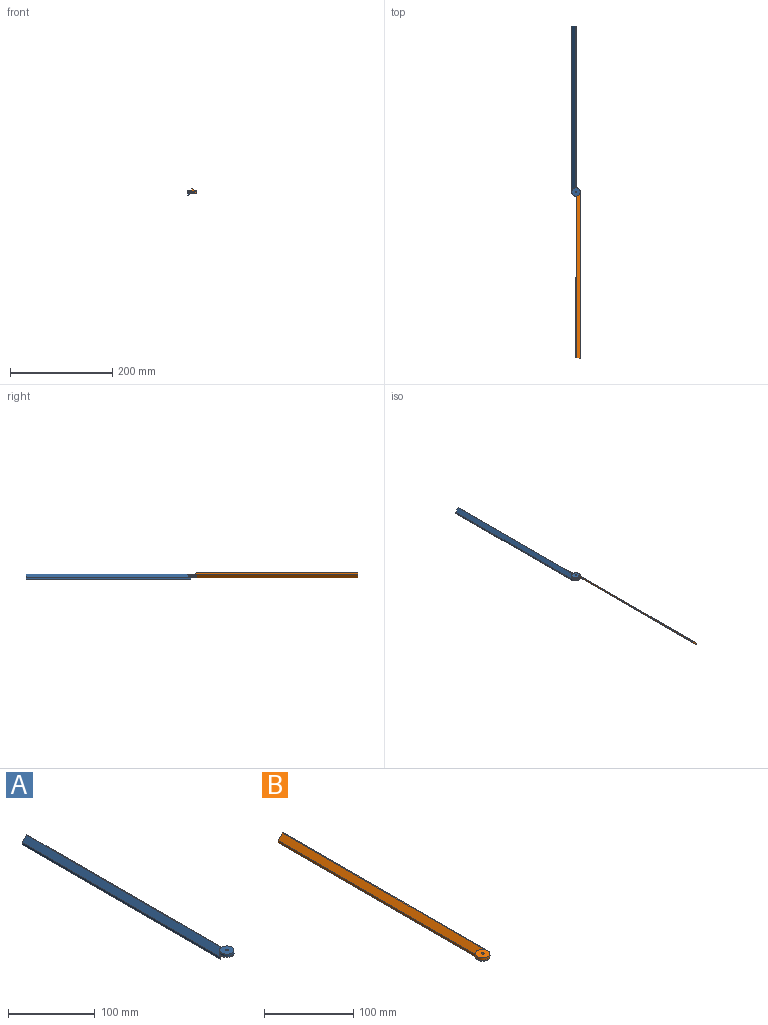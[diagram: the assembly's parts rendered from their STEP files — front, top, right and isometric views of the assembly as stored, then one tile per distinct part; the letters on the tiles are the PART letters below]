
ASSEMBLY  parts=2 mates=1
PART A: 69 faces, bbox 16.5x333.2x10 mm
  f0: plane 320.63x7mm, normal (0.71,0,-0.71), area 3147.1mm2, adj f2,f14,f17,f18,f22,f23,f25,f55
  f1: plane 322.98x7mm, normal (-0.71,0,0.71), area 3153.9mm2, adj f2,f18,f21,f23,f24,f32,f57,f58
  f2: cylinder r=8.24mm len=16.47mm, axis (0,0,-1), area 197.9mm2, adj f0,f1,f3,f4,f5,f6,f7,f8
  f3: plane 0.02x0.01mm, normal (0,0,-1), area 0mm2, adj f2,f28,f29
  f4: plane 0.03x0.01mm, normal (0,0,-1), area 0mm2, adj f2,f27,f30
  f5: plane 0.01x0.01mm, normal (0,0,-1), area 0mm2, adj f2,f31,f35
  f6: plane 0x0mm, normal (0,0,-1), area 0mm2, adj f2,f36,f37
  f7: plane 0x0mm, normal (0,0,-1), area 0mm2, adj f2,f42,f43
  f8: plane 0.01x0.01mm, normal (0,0,-1), area 0mm2, adj f2,f44,f45
  f9: plane 0.02x0.01mm, normal (0,0,-1), area 0mm2, adj f2,f46,f47
  f10: plane 0.03x0.02mm, normal (0,0,-1), area 0mm2, adj f2,f48,f49
  f11: plane 0.04x0.04mm, normal (0,0,-1), area 0mm2, adj f2,f50,f51
  f12: plane 0.05x0.03mm, normal (0,0,-1), area 0mm2, adj f2,f52,f53
  f13: plane 0.06x0.02mm, normal (0,0,-1), area 0mm2, adj f2,f54,f55
  f14: plane 0.03x0.01mm, normal (0,0,-1), area 0mm2, adj f0,f17,f62
  f15: plane 0.71x0.48mm, normal (0,0,-1), area 0mm2, adj f18,f63
  f16: plane 0.04x0.03mm, normal (0,0,-1), area 0mm2, adj f2,f33,f34
  f17: cylinder r=8.25mm len=0.03mm, axis (0,0,1), area 0mm2, adj f0,f14,f62
  f18: cylinder r=8.25mm len=5.97mm, axis (0,0,1), area 25.1mm2, adj f0,f1,f15,f21,f25,f26,f59,f60
  f19: plane 3.45x2.32mm, normal (1,0,0), area 7.6mm2, adj f20,f24,f27,f28,f29,f30,f31,f32
  f20: cylinder r=1.6mm len=3.46mm, axis (0,0,1), area 24.4mm2, adj f19,f24,f35,f36,f37,f38,f39,f40
  f21: plane 322.98x3mm, normal (-1,0,0), area 968.9mm2, adj f1,f18,f23,f25
  f22: plane 316.76x3mm, normal (1,0,0), area 950.3mm2, adj f0,f2,f23,f24
  f23: plane 10x8mm, normal (0,1,0), area 31mm2, adj f0,f1,f21,f22,f24,f25
  f24: plane 333.24x16.47mm, normal (0,0,1), area 522.6mm2, adj f1,f2,f19,f20,f22,f23
  f25: plane 322.98x1mm, normal (0,0,-1), area 321.6mm2, adj f0,f18,f21,f23
  f26: plane 1.02x0.82mm, normal (0,0,1), area 0.1mm2, adj f18,f59,f63
  f27: plane 7.14x1.91mm, normal (0.15,-0.75,-0.64), area 10.2mm2, adj f2,f4,f19,f28,f30
  f28: plane 6.98x2.93mm, normal (-0.15,0.75,-0.64), area 10.2mm2, adj f2,f3,f19,f27,f29
  f29: plane 6.51x4.12mm, normal (0.43,-0.64,-0.64), area 10.1mm2, adj f2,f3,f19,f28,f31
  f30: plane 7.14x1.91mm, normal (0.15,0.75,-0.64), area 10.2mm2, adj f2,f4,f19,f27,f34
  f31: plane 5.75x5.09mm, normal (-0.43,0.64,-0.64), area 10mm2, adj f2,f5,f19,f29,f35
  f32: plane 5.75x5.21mm, normal (-0.43,-0.64,-0.64), area 10.1mm2, adj f1,f2,f19,f33,f58,f64,f65,f66
  f33: plane 6.5x4.12mm, normal (0.43,0.64,-0.64), area 10.1mm2, adj f2,f16,f19,f32,f34
  f34: plane 6.98x2.93mm, normal (-0.15,-0.75,-0.64), area 10.2mm2, adj f2,f16,f19,f30,f33
  f35: plane 5.75x4.94mm, normal (0.64,-0.43,-0.64), area 10mm2, adj f2,f5,f19,f20,f31,f36
  f36: plane 6.28x3.96mm, normal (-0.64,0.43,-0.64), area 10mm2, adj f2,f6,f20,f35,f37
  f37: plane 6.6x2.84mm, normal (0.75,-0.15,-0.64), area 10mm2, adj f2,f6,f20,f36,f38
  f38: plane 6.67x1.92mm, normal (-0.75,0.15,-0.64), area 10mm2, adj f2,f20,f37,f39
  f39: plane 6.67x1.92mm, normal (0.75,0.15,-0.64), area 10mm2, adj f2,f20,f38,f40
  f40: plane 6.6x2.84mm, normal (-0.75,-0.15,-0.64), area 10mm2, adj f2,f20,f39,f41
  f41: plane 6.28x3.97mm, normal (0.64,0.42,-0.64), area 10mm2, adj f2,f20,f40,f42
  f42: plane 5.72x4.93mm, normal (-0.64,-0.43,-0.64), area 10mm2, adj f2,f7,f20,f41,f43
  f43: plane 5.72x4.94mm, normal (0.43,0.64,-0.64), area 10mm2, adj f2,f7,f20,f42,f44
  f44: plane 6.28x3.96mm, normal (-0.43,-0.64,-0.64), area 10mm2, adj f2,f8,f20,f43,f45
  f45: plane 6.6x2.84mm, normal (0.15,0.75,-0.64), area 10mm2, adj f2,f8,f20,f44,f46
  f46: plane 6.67x1.91mm, normal (-0.15,-0.75,-0.64), area 10mm2, adj f2,f9,f20,f45,f47
  f47: plane 6.67x1.91mm, normal (-0.15,0.75,-0.64), area 10mm2, adj f2,f9,f20,f46,f48
  f48: plane 6.6x2.83mm, normal (0.15,-0.75,-0.64), area 10mm2, adj f2,f10,f20,f47,f49
  f49: plane 6.28x3.97mm, normal (-0.43,0.64,-0.64), area 10mm2, adj f2,f10,f20,f48,f50
  f50: plane 5.72x4.93mm, normal (0.43,-0.64,-0.64), area 10mm2, adj f2,f11,f20,f49,f51
  f51: plane 5.72x4.93mm, normal (-0.64,0.42,-0.64), area 10mm2, adj f2,f11,f20,f50,f52
  f52: plane 6.27x3.96mm, normal (0.64,-0.43,-0.64), area 10mm2, adj f2,f12,f20,f51,f53
  f53: plane 6.6x2.84mm, normal (-0.75,0.15,-0.64), area 10mm2, adj f2,f12,f20,f52,f54
  f54: plane 6.67x1.91mm, normal (0.75,-0.15,-0.64), area 10mm2, adj f2,f13,f20,f53,f55
  f55: plane 6.67x1.91mm, normal (-0.75,-0.15,-0.64), area 10mm2, adj f0,f2,f13,f20,f54,f56,f62
  f56: plane 6.61x2.91mm, normal (0.75,0.15,-0.64), area 10.1mm2, adj f20,f55,f57,f62,f67,f68
  f57: plane 6.44x3.97mm, normal (-0.64,-0.43,-0.64), area 10.1mm2, adj f1,f2,f20,f56,f58,f63,f67,f68
  f58: plane 5.75x5.06mm, normal (0.64,0.43,-0.64), area 10mm2, adj f1,f2,f19,f20,f32,f57,f63,f65
  f59: plane 0.36x0.21mm, normal (0,0,1), area 0mm2, adj f1,f18,f26,f64
  f60: plane 1.04x0.68mm, normal (0,0,1), area 0.1mm2, adj f18,f61,f63
  f61: plane 1.17x0.39mm, normal (0,0,1), area 0.1mm2, adj f18,f60,f62
  f62: plane 2.29x1.97mm, normal (0.2,-0.98,0), area 2mm2, adj f0,f14,f17,f55,f56,f61
  f63: plane 2.74x1.83mm, normal (0.56,-0.83,0), area 2.8mm2, adj f1,f15,f18,f26,f57,f58,f60
  f64: plane 0.19x0.13mm, normal (0.83,-0.56,0), area 0mm2, adj f1,f32,f59
  f65: cylinder r=8.25mm len=0.02mm, axis (0,0,1), area 0mm2, adj f32,f58,f66
  f66: plane 0.06x0.06mm, normal (0,0,-1), area 0mm2, adj f32,f58,f65
  f67: cylinder r=8.25mm len=0.03mm, axis (0,0,1), area 0mm2, adj f56,f57,f68
  f68: plane 0.07x0.04mm, normal (0,0,-1), area 0mm2, adj f56,f57,f67
PART B: 63 faces, bbox 16.9x333.7x10.5 mm
  f0: cylinder r=8.24mm len=16.47mm, axis (0,0,-1), area 189.1mm2, adj f2,f3,f5,f7,f13,f14,f15,f16
  f1: cylinder r=8.24mm len=1.48mm, axis (0,0,-1), area 0.7mm2, adj f3,f24,f25
  f2: plane 321.12x7.46mm, normal (-0.71,0,0.71), area 3147.1mm2, adj f0,f4,f6,f7,f9,f10,f47
  f3: plane 323.49x7.45mm, normal (0.71,0,-0.71), area 3153.9mm2, adj f0,f1,f5,f6,f8,f9,f10,f45
  f4: plane 316.75x3mm, normal (-1,0,0), area 950.2mm2, adj f2,f6,f8,f10
  f5: plane 323.04x3mm, normal (1,0,0), area 969.1mm2, adj f0,f3,f6,f7
  f6: plane 10x8mm, normal (0,1,0), area 31mm2, adj f2,f3,f4,f5,f7,f8
  f7: plane 333.24x16.47mm, normal (0,0,1), area 527.5mm2, adj f0,f2,f5,f6,f11,f12
  f8: plane 316.81x1mm, normal (0,0,-1), area 316.8mm2, adj f3,f4,f6,f10
  f9: plane 4x2.36mm, normal (0,0,-1), area 0.1mm2, adj f2,f3,f10,f26,f27,f46,f47
  f10: cylinder r=8.25mm len=6mm, axis (0,0,1), area 17.3mm2, adj f2,f3,f4,f8,f9
  f11: plane 3.4x2.32mm, normal (1,0,0), area 7.5mm2, adj f7,f12,f13,f14,f15,f16,f17,f18
  f12: cylinder r=1.6mm len=3.47mm, axis (0,0,1), area 24.5mm2, adj f7,f11,f21,f22,f23,f24,f25,f26
  f13: plane 5.76x5.1mm, normal (0.54,0.54,-0.64), area 10mm2, adj f0,f11,f14,f33,f56
  f14: plane 6.52x4.13mm, normal (-0.29,-0.71,-0.64), area 10.1mm2, adj f0,f11,f13,f15,f56
  f15: plane 6.99x2.94mm, normal (0.29,0.71,-0.64), area 10.2mm2, adj f0,f11,f14,f16,f55
  f16: plane 7.15x1.92mm, normal (0,-0.77,-0.64), area 10.2mm2, adj f0,f11,f15,f17,f55
  f17: plane 7.15x1.92mm, normal (0,0.77,-0.64), area 10.2mm2, adj f0,f11,f16,f18,f54
  f18: plane 6.99x2.94mm, normal (0.29,-0.71,-0.64), area 10.2mm2, adj f0,f11,f17,f19,f54
  f19: plane 6.52x4.13mm, normal (-0.29,0.71,-0.64), area 10.1mm2, adj f0,f11,f18,f20,f53
  f20: plane 5.76x5.1mm, normal (0.54,-0.54,-0.64), area 10mm2, adj f0,f11,f19,f35,f53
  f21: plane 6.68x1.92mm, normal (0,0.77,-0.64), area 10mm2, adj f0,f12,f22,f34,f57
  f22: plane 6.68x1.92mm, normal (0,-0.77,-0.64), area 10mm2, adj f0,f12,f21,f23,f62
  f23: plane 6.61x2.85mm, normal (-0.29,0.71,-0.64), area 10mm2, adj f0,f12,f22,f24,f45,f62
  f24: plane 6.29x3.97mm, normal (0.29,-0.71,-0.64), area 10mm2, adj f1,f12,f23,f25,f45,f61
  f25: plane 5.72x4.94mm, normal (-0.54,0.54,-0.64), area 10mm2, adj f1,f12,f24,f26,f46,f61
  f26: plane 5.72x4.94mm, normal (0.54,-0.54,-0.64), area 10mm2, adj f9,f12,f25,f27,f46
  f27: plane 6.29x3.96mm, normal (-0.71,0.29,-0.64), area 10mm2, adj f0,f9,f12,f26,f28,f47
  f28: plane 6.61x2.85mm, normal (0.71,-0.29,-0.64), area 10mm2, adj f0,f12,f27,f29,f60
  f29: plane 6.68x1.92mm, normal (-0.77,0,-0.64), area 10mm2, adj f0,f12,f28,f30,f60
  f30: plane 6.68x1.92mm, normal (0.77,0,-0.64), area 10mm2, adj f0,f12,f29,f31,f59
  f31: plane 6.61x2.85mm, normal (-0.71,-0.29,-0.64), area 10mm2, adj f0,f12,f30,f32,f59
  f32: plane 6.29x3.97mm, normal (0.71,0.29,-0.64), area 10mm2, adj f0,f12,f31,f33,f58
  f33: plane 5.76x4.94mm, normal (-0.54,-0.54,-0.64), area 10mm2, adj f0,f11,f12,f13,f32,f58
  f34: plane 6.61x2.85mm, normal (-0.29,-0.71,-0.64), area 10mm2, adj f0,f12,f21,f44,f57
  f35: plane 5.76x4.94mm, normal (-0.54,0.54,-0.64), area 10mm2, adj f0,f11,f12,f20,f36,f52
  f36: plane 6.29x3.97mm, normal (0.71,-0.29,-0.64), area 10mm2, adj f0,f12,f35,f37,f52
  f37: plane 6.61x2.85mm, normal (-0.71,0.29,-0.64), area 10mm2, adj f0,f12,f36,f38,f51
  f38: plane 6.68x1.92mm, normal (0.77,0,-0.64), area 10mm2, adj f0,f12,f37,f39,f51
  f39: plane 6.68x1.92mm, normal (-0.77,0,-0.64), area 10mm2, adj f0,f12,f38,f40,f50
  f40: plane 6.61x2.85mm, normal (0.71,0.29,-0.64), area 10mm2, adj f0,f12,f39,f41,f50
  f41: plane 6.29x3.97mm, normal (-0.71,-0.29,-0.64), area 10mm2, adj f0,f12,f40,f42,f49
  f42: plane 5.72x4.94mm, normal (0.54,0.54,-0.64), area 10mm2, adj f0,f12,f41,f43,f49
  f43: plane 5.72x4.94mm, normal (-0.54,-0.54,-0.64), area 10mm2, adj f0,f12,f42,f44,f48
  f44: plane 6.29x3.97mm, normal (0.29,0.71,-0.64), area 10mm2, adj f0,f12,f34,f43,f48
  f45: cylinder r=8.24mm len=0.52mm, axis (0,0,-1), area 0.1mm2, adj f3,f23,f24
  f46: cylinder r=8.24mm len=1.98mm, axis (0,0,-1), area 2.7mm2, adj f3,f9,f25,f26
  f47: cylinder r=8.24mm len=2.57mm, axis (0,0,-1), area 2.1mm2, adj f2,f9,f27
  f48: plane 0.03x0.03mm, normal (0,0,-1), area 0mm2, adj f43,f44
  f49: plane 0.03x0.03mm, normal (0,0,-1), area 0mm2, adj f41,f42
  f50: plane 0.04x0.01mm, normal (0,0,-1), area 0mm2, adj f39,f40
  f51: plane 0.04x0.01mm, normal (0,0,-1), area 0mm2, adj f37,f38
  f52: plane 0.03x0.03mm, normal (0,0,-1), area 0mm2, adj f35,f36
  f53: plane 0.03x0.03mm, normal (0,0,-1), area 0mm2, adj f19,f20
  f54: plane 0.04x0.01mm, normal (0,0,-1), area 0mm2, adj f17,f18
  f55: plane 0.04x0.01mm, normal (0,0,-1), area 0mm2, adj f15,f16
  f56: plane 0.03x0.03mm, normal (0,0,-1), area 0mm2, adj f13,f14
  f57: plane 0.04x0.01mm, normal (0,0,-1), area 0mm2, adj f21,f34
  f58: plane 0.03x0.03mm, normal (0,0,-1), area 0mm2, adj f32,f33
  f59: plane 0.04x0.01mm, normal (0,0,-1), area 0mm2, adj f30,f31
  f60: plane 0.04x0.01mm, normal (0,0,-1), area 0mm2, adj f28,f29
  f61: plane 0.03x0.03mm, normal (0,0,-1), area 0mm2, adj f24,f25
  f62: plane 0.04x0.01mm, normal (0,0,-1), area 0mm2, adj f22,f23
PLACE A t=(-3.17,0.08,1.41)mm
PLACE B rot(axis=(1,0,0),180deg) t=(-3.17,0.08,14.5)mm
MATE slider A.f24 <-> B.f7  axis (0,0,1) through (-4.27,-1.08,11.41)mm
